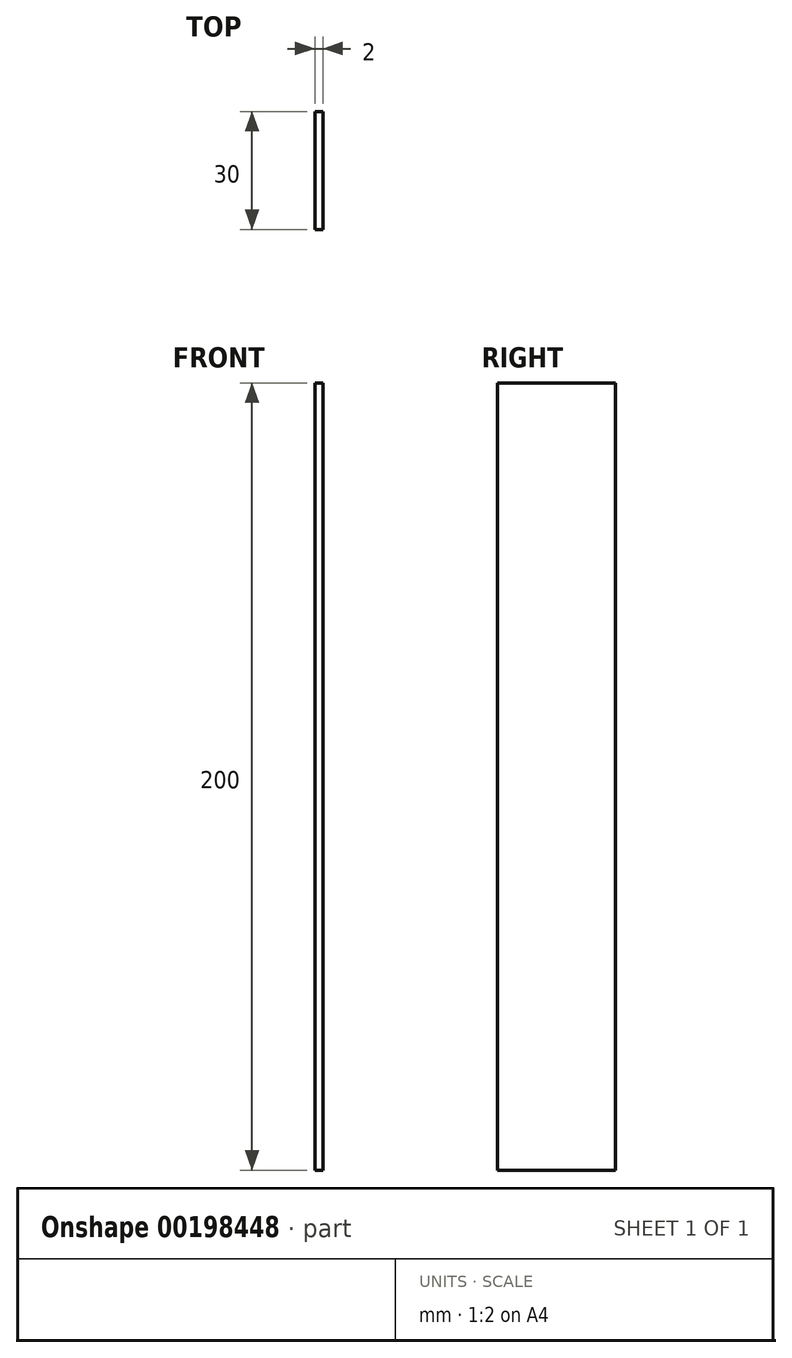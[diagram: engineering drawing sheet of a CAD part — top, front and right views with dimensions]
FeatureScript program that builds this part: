
annotation { "Feature Type Name" : "Feature", "Feature Type Description" : "" }
export const myFeature = defineFeature(function(context is Context, id is Id, definition is map)
    precondition{}
    {
        {
            var Q0;
            Q0=qCreatedBy(makeId("Right.planeOp"),FACE);
            var sketch = newSketch(context, id + "F0", { "sketchPlane" : qUnion([Q0])});
            skLineSegment(sketch, "E0.bottom", {"start": v(0, 0) * mm, "end": v(30, 0) * mm});
            skLineSegment(sketch, "E0.top", {"start": v(0, 200) * mm, "end": v(30, 200) * mm});
            skLineSegment(sketch, "E0.left", {"start": v(0, 0) * mm, "end": v(0, 200) * mm});
            skLineSegment(sketch, "E0.right", {"start": v(30, 0) * mm, "end": v(30, 200) * mm});
            skSolve(sketch);
        }
        {
            var Q0;
            Q0=makeQuery(id+"F0.imprint","IMPRINT",FACE,{"disambiguationData":[TD([[makeQuery(id+"F0.imprint","IMPRINT",EDGE,{"derivedFrom":sQuery(id+"F0.wireOp",EDGE,"E0.bottom")}),1.0]])]});
            extrude(context, id + "F1", {"entities" : qUnion([Q0]), "depth" : 2 * mm});
        }
    });
